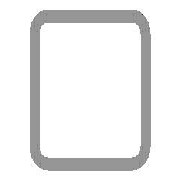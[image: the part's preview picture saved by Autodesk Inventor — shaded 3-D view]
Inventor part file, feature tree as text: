
AUTODESK INVENTOR PART (.ipt)
format: ipt  version: 2022 (Build 260153000, 153)  size: 182,272 bytes
history: native  units: mm (DEFAULTED — no unit token found)
features: other x5, sketch x2, sweep x1, plane x1
ambient origin geometry x8: Origin, YZ Plane, XZ Plane, XY Plane, X Axis, Y Axis, Z Axis, Center Point
bodies: Solid1 (feature_tree), Body (feature_tree)
feature tree (9):
  parser-record x1  (decoder bookkeeping rows leaked as tree rows — omitted from the tree; the rows remain in map.json)
  other  "Driven Length"
  other  "Start Plane"
  other  "End Plane"
  sweep  "Sweep Path"
  other  "Orientation Work Plane"
  sketch  "Sketch3"  dims[d7=7.5mm d10=40.0mm]
  plane  "Work Plane3"
  sketch  "Sketch4"  dims[d11=40.0mm d12=5.0mm d13=-0.0mm d14=2815.406592mm d15=20.0mm d16=20.0mm d17=90.0deg d18=2815.406592mm d19=0.0mm d20=0.0mm]
